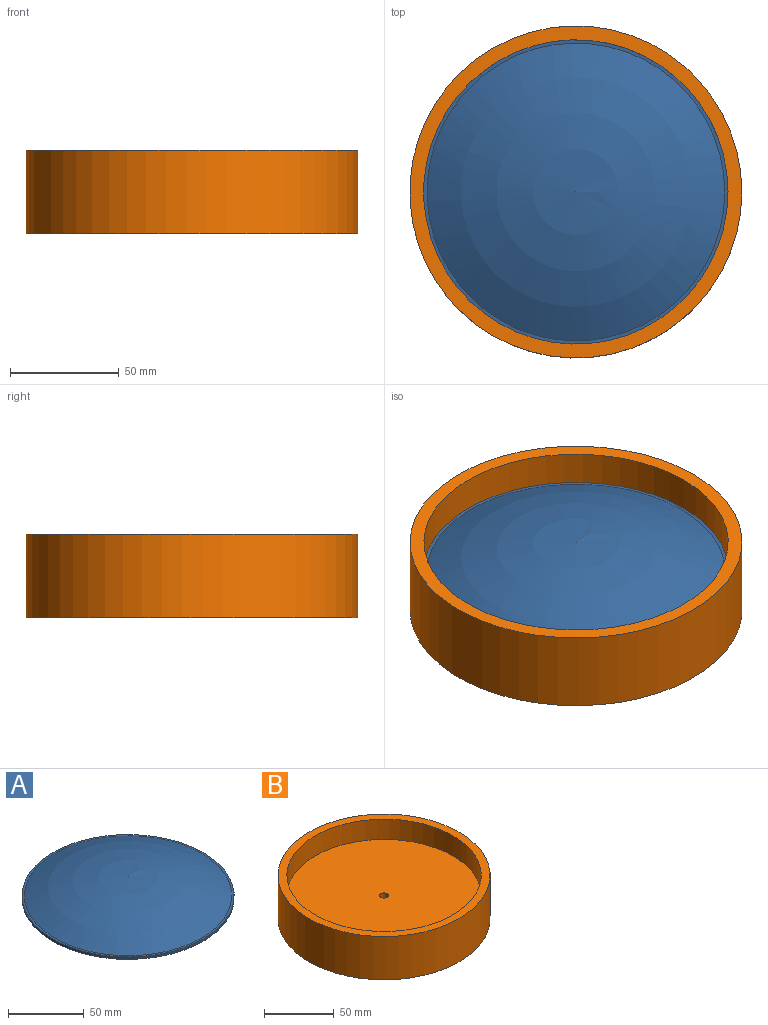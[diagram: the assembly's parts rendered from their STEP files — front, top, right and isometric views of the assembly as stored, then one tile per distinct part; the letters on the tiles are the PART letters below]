
ASSEMBLY  parts=2 mates=1
PART A: 5 faces, bbox 139.7x139.7x17.8 mm
  f0: plane 139.7x139.7mm, normal (0,0,1), area 661.6mm2, adj f1,f4
  f1: cylinder r=69.85mm len=139.7mm, axis (0,0,1), area 836.1mm2, adj f0,f2
  f2: plane 139.7x139.7mm, normal (0,0,-1), area 3702mm2, adj f1,f3
  f3: torus R=3.12mm, axis (0,0,1), area 12150.2mm2, adj f2
  f4: torus R=3.56mm, axis (0,0,1), area 15520.3mm2, adj f0
PART B: 8 faces, bbox 152.4x152.4x38.1 mm
  f0: cylinder r=76.2mm len=152.4mm, axis (0,0,-1), area 18185.5mm2, adj f1,f2,f5
  f1: plane 152.4x152.4mm, normal (0,0,1), area 2913.6mm2, adj f0,f3
  f2: plane 152.4x152.4mm, normal (0,0,-1), area 18241.5mm2, adj f0
  f3: cylinder r=69.85mm len=139.7mm, axis (0,0,1), area 7803.3mm2, adj f1,f4
  f4: plane 139.7x139.7mm, normal (0,0,1), area 15296.2mm2, adj f3,f7
  f5: cylinder r=4.22mm len=82.55mm, axis (0,-1,0), area 2150.8mm2, adj f0,f6,f7
  f6: plane 8.43x8.43mm, normal (0,1,0), area 55.9mm2, adj f5
  f7: cylinder r=3.17mm len=7.39mm, axis (0,0,1), area 132.2mm2, adj f4,f5
PLACE A t=(-36,52.71,101.33)mm
PLACE B t=(-36,52.71,81.01)mm
MATE fastened B.f3 <-> A.f1  axis (0,0,1) through (-36,52.71,101.33)mm
